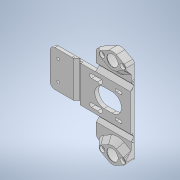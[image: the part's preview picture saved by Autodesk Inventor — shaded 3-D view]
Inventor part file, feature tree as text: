
AUTODESK INVENTOR PART (.ipt)
format: ipt  version: 2022 (Build 260153000, 153)  size: 981,504 bytes
history: native  units: in
note: dims shown in document units (in); Inventor stores cm internally (conversion verified against a paired STEP export)
features: projected_geometry x37, sketch x23, extrude x16, other x7, sheet_metal_op x7, move_body x7, plane x5, boolean_combine x4, split x4, hole x2, chamfer x2, mirror x2, fillet x1, direct_edit x1
ambient origin geometry x8: Origin, YZ Plane, XZ Plane, XY Plane, X Axis, Y Axis, Z Axis, Center Point
bodies: Solid3 (feature_tree), Solid2 (feature_tree), Solid6 (feature_tree), Solid7 (feature_tree), Solid8 (feature_tree), Solid9 (feature_tree), Solid10 (feature_tree), Solid11 (feature_tree)
feature tree (118):
  other  "Z Drive Bearing Holder.ipt"
  sheet_metal_op  "Face1"
  sheet_metal_op  "Flange2"
  sketch  "Sketch3"  dims[d1=2.1654in d4=1.2205in]
  hole  "Hole2"  [1 undecoded]
  sheet_metal_op  "Flange3"
  chamfer  "Corner Round2"
  hole  "Hole3"  [1 undecoded]
  extrude  "Extrusion3"  Depth=1.2205in
  extrude  "Extrusion4"  Depth=0.1969in
  extrude  "Extrusion5"  Depth=0.1969in
  extrude  "Extrusion7"  Depth=0.08in
  extrude  "Extrusion8"  Depth=0.08in
  extrude  "Extrusion9"  Depth=0.315in
  extrude  "Extrusion10"  Depth=0.4921in
  plane  "Work Plane2"
  mirror  "Mirror2"
  move_body  "Move Body2"
  move_body  "Move Body3"
  move_body  "Move Body8"
  boolean_combine  "Combine1"
  extrude  "Extrusion11"  Depth=0.1969in
  extrude  "Extrusion12"  Depth=0.08in
  extrude  "Extrusion15"  Depth=1.2205in
  fillet  "Fillet3"  Radius=0.08in
  chamfer  "Chamfer1"  Distance=1.2205in Angle=90.0deg
  plane  "Work Plane6"
  extrude  "Extrusion20"  Depth=0.08in
  extrude  "Extrusion21"  Depth=0.3937in
  split  "Split3"
  mirror  "Mirror4"
  plane  "Work Plane7"
  plane  "Work Plane8"
  plane  "Work Plane9"
  split  "Split4"
  split  "Split5"
  split  "Split6"
  sketch  "Sketch30"  dims[d99=0.08in d100=0.04in]
  sketch  "Sketch31"  dims[d101=0.16in d102=0.08in]
  sketch  "Sketch32"  dims[d103=1.2205in d104=90.0deg d105=0.08in d106=0.32in]
  move_body  "Move Body10"
  move_body  "Move Body11"
  move_body  "Move Body12"
  boolean_combine  "Combine3"
  boolean_combine  "Combine4"
  boolean_combine  "Combine5"
  extrude  "Extrusion22"  Depth=0.2362in
  extrude  "Extrusion23"  Depth=0.04in
  extrude  "Extrusion24"  Depth=0.08in
  extrude  "Extrusion25"  Depth=1.2205in
  direct_edit  "Direct Edit1"
  other  "Plate1"
  sketch  "Sketch6"  dims[d7=1.2205in d8=1.2205in]
  other  "Plate4"
  sheet_metal_op  "Bend3"
  sheet_metal_op  "Corner2"
  sketch  "Sketch7"  dims[d9=1.2205in d10=1.2205in]
  other  "Plate5"
  sheet_metal_op  "Bend4"
  sheet_metal_op  "Corner3"
  sketch  "Sketch8"  dims[d11=0.0669in d12=0.1969in]
  sketch  "Sketch9"  dims[d13=0.4528in d14=0.1969in]
  projected_geometry  "Projected Loop2"
  projected_geometry  "Projected Loop3"
  sketch  "Sketch10"  dims[d15=0.5906in d16=0.08in]
  projected_geometry  "Projected Loop4"
  sketch  "Sketch11"  dims[d36=0.5512in d41=0.08in]
  projected_geometry  "Projected Loop5"
  projected_geometry  "Projected Loop6"
  projected_geometry  "Projected Loop7"
  projected_geometry  "Projected Loop8"
  sketch  "Sketch12"  dims[d42=0.0in]
  projected_geometry  "Projected Loop9"
  projected_geometry  "Projected Loop10"
  projected_geometry  "Projected Loop11"
  projected_geometry  "Projected Loop12"
  sketch  "Sketch13"  dims[d43=0.1339in d44=0.2362in d45=0.2559in d46=0.1181in d47=90.0deg d48=0.315in d49=0.8108in d53=2.4803in]
  projected_geometry  "Projected Loop13"
  sketch  "Sketch14"  dims[d55=0.4921in d56=0.4921in]
  projected_geometry  "Projected Loop14"
  projected_geometry  "Projected Loop15"
  projected_geometry  "Projected Loop16"
  projected_geometry  "Projected Loop17"
  sketch  "Sketch15"  dims[d83=1.6929in d84=0.1969in]
  projected_geometry  "Projected Loop18"
  projected_geometry  "Projected Loop19"
  projected_geometry  "Projected Loop20"
  projected_geometry  "Projected Loop21"
  projected_geometry  "Projected Loop22"
  other  "Solid1::Z Drive Bearing Holder.ipt"
  other  "TaggingFeature1"
  sketch  "Sketch16"  dims[d85=0.5512in d86=0.08in]
  projected_geometry  "Projected Loop23"
  sketch  "Sketch17"  dims[d87=0.04in d88=0.16in d89=0.08in d90=1.2205in d91=90.0deg d92=0.08in]
  projected_geometry  "Projected Loop24"
  sketch  "Sketch20"  dims[d93=0.32in d94=0.08in]
  projected_geometry  "Projected Loop27"
  projected_geometry  "Projected Loop28"
  sketch  "Sketch27"  dims[d95=0.08in d96=0.3937in]
  projected_geometry  "Projected Loop38"
  projected_geometry  "Projected Loop39"
  projected_geometry  "Projected Loop40"
  sketch  "Sketch28"  dims[d97=0.1575in d98=0.2362in]
  projected_geometry  "Projected Loop41"
  projected_geometry  "Projected Loop42"
  sketch  "Sketch34"  dims[d107=0.08in]
  projected_geometry  "Projected Loop46"
  projected_geometry  "Projected Loop47"
  sketch  "Sketch35"  dims[d108=0.08in]
  projected_geometry  "Projected Loop48"
  projected_geometry  "Projected Loop49"
  sketch  "Sketch36"  dims[d109=0.3937in]
  projected_geometry  "Projected Loop50"
  projected_geometry  "Projected Loop51"
  sketch  "Sketch37"  dims[d110=0.3937in d111=0.3937in d112=0.1339in d113=0.2362in d114=0.2559in d115=0.1181in d116=0.6181in d117=0.08in d118=0.8108in d119=0.3937in d120=0.0in d121=0.3937in d122=0.0in d123=0.1575in d124=0.3937in d125=0.0in d128=0.3937in d129=0.0in d130=0.0787in d131=0.0in d132=0.1575in d133=0.0787in d134=0.0in d135=0.3937in d136=0.0in d138=0.3937in d142=90.0deg d143=90.0deg d156=0.3937in d157=0.0in d158=0.3937in d159=0.0in d160=1.9907in d161=-0.8636in d162=-0.2362in d167=0.4188in d168=0.0in d169=0.1969in d172=0.2555in d173=0.0787in d174=45.0deg d185=0.0in d186=0.0in d187=0.0in d188=0.0in d189=-0.6184in d190=-0.6184in d191=90.0deg d194=0.0079in d195=1.6929in d196=0.0in d197=0.0079in d198=1.6929in d199=0.0in d200=0.0079in d201=1.6929in d202=0.0in d203=0.1969in d204=0.1969in d205=0.2756in d206=0.1969in d207=0.1969in d208=0.2756in d209=0.1969in d210=0.0in d211=0.0in d212=0.0in d213=0.0in d214=0.0315in]
  projected_geometry  "Projected Loop52"
  other  "Cut1"
  move_body  "Move1"
note: 2 required parameter values undecoded (feature->parameter linkage not recoverable at this tier; creation-order binding heuristic only, values carry confidence <= 0.55)
